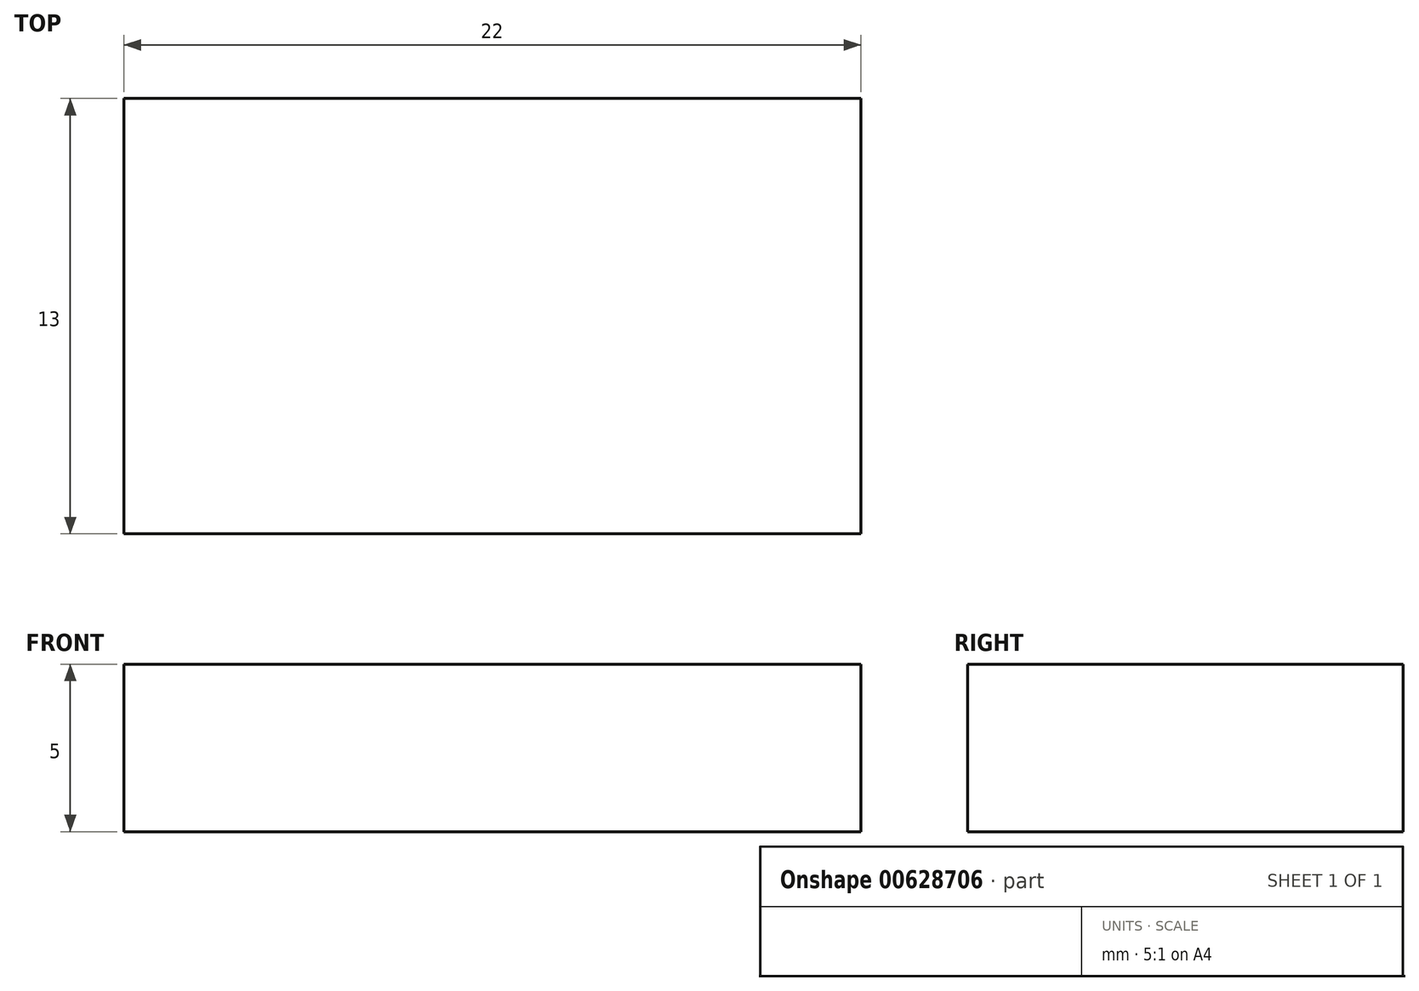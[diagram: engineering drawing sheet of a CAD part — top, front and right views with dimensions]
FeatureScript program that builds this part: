
annotation { "Feature Type Name" : "Feature", "Feature Type Description" : "" }
export const myFeature = defineFeature(function(context is Context, id is Id, definition is map)
    precondition{}
    {
        {
            var Q0;
            Q0=qCreatedBy(makeId("Top.planeOp"),FACE);
            var sketch = newSketch(context, id + "F0", { "sketchPlane" : qUnion([Q0])});
            skLineSegment(sketch, "E0.bottom", {"start": v(11, 6.5) * mm, "end": v(-11, 6.5) * mm});
            skLineSegment(sketch, "E0.top", {"start": v(11, -6.5) * mm, "end": v(-11, -6.5) * mm});
            skLineSegment(sketch, "E0.left", {"start": v(11, 6.5) * mm, "end": v(11, -6.5) * mm});
            skLineSegment(sketch, "E0.right", {"start": v(-11, 6.5) * mm, "end": v(-11, -6.5) * mm});
            skPoint(sketch, "E0.middle", {"position": v(0, 0) * mm});
            skSolve(sketch);
        }
        {
            var Q0;
            Q0 = qSketchRegion(id + "F0", true);
            extrude(context, id + "F1", {"entities" : qUnion([Q0]), "endBound" : BoundingType.SYMMETRIC, "depth" : 5 * mm, "offsetDistance" : 25 * mm});
        }
    });
